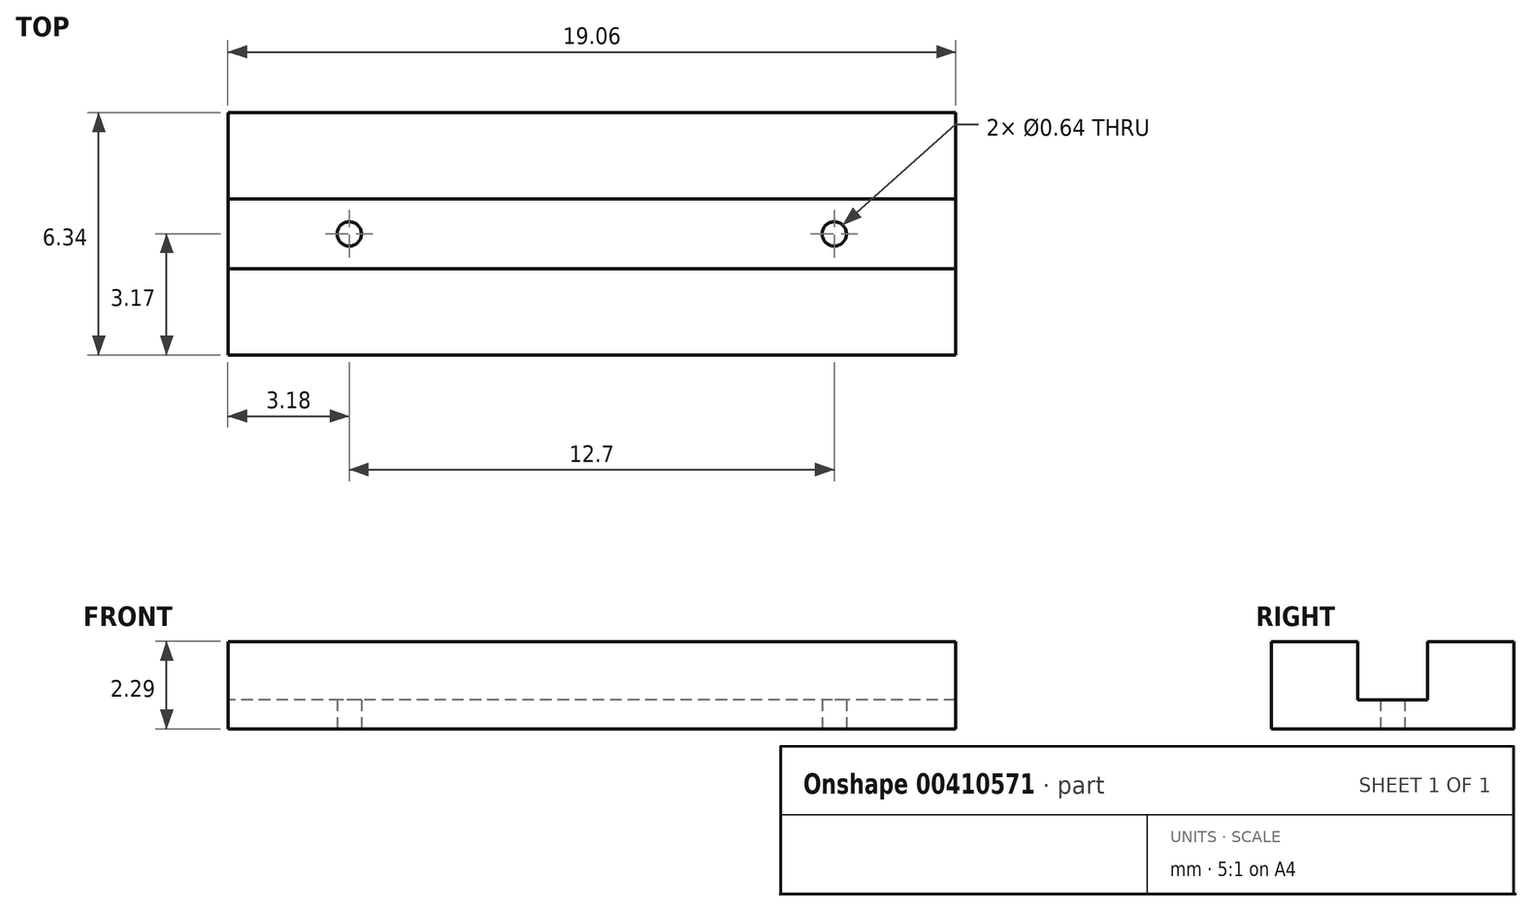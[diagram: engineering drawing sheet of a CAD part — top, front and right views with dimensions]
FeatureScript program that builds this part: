
annotation { "Feature Type Name" : "Feature", "Feature Type Description" : "" }
export const myFeature = defineFeature(function(context is Context, id is Id, definition is map)
    precondition{}
    {
        {
            var Q0;
            Q0=qCreatedBy(makeId("Top.planeOp"),FACE);
            var sketch = newSketch(context, id + "F0", { "sketchPlane" : qUnion([Q0])});
            skLineSegment(sketch, "E0.bottom", {"start": v(9.53, 3.18) * mm, "end": v(-9.53, 3.18) * mm});
            skLineSegment(sketch, "E0.top", {"start": v(9.53, -3.18) * mm, "end": v(-9.53, -3.18) * mm});
            skLineSegment(sketch, "E0.left", {"start": v(9.53, 3.17) * mm, "end": v(9.53, -3.18) * mm});
            skLineSegment(sketch, "E0.right", {"start": v(-9.53, 3.17) * mm, "end": v(-9.53, -3.18) * mm});
            skPoint(sketch, "E0.middle", {"position": v(0, 0) * mm});
            skLineSegment(sketch, "E1.bottom", {"start": v(9.53, 0.91) * mm, "end": v(-9.53, 0.91) * mm});
            skLineSegment(sketch, "E1.top", {"start": v(9.53, -0.91) * mm, "end": v(-9.53, -0.91) * mm});
            skLineSegment(sketch, "E1.left", {"start": v(9.53, 0.91) * mm, "end": v(9.53, -0.91) * mm});
            skLineSegment(sketch, "E1.right", {"start": v(-9.53, 0.91) * mm, "end": v(-9.53, -0.91) * mm});
            skCircle(sketch, "E2", {"center": v(6.35, 0) * mm, "radius": 0.32 * mm});
            skCircle(sketch, "E3", {"center": v(-6.35, 0) * mm, "radius": 0.32 * mm});
            skSolve(sketch);
        }
        {
            var Q0;
            Q0=makeQuery(id+"F0.imprint","IMPRINT",FACE,{"disambiguationData":[TD([[makeQuery(id+"F0.imprint","IMPRINT",EDGE,{"derivedFrom":sQuery(id+"F0.wireOp",EDGE,"E1.bottom")}),1.0]])]});
            extrude(context, id + "F1", {"entities" : qUnion([Q0]), "depth" : 0.76 * mm});
        }
        {
            var Q0;
            {var subQ0=sQuery(id+"F0.wireOp",EDGE,"E0.top");Q0=makeQuery(id+"F0.imprint","IMPRINT",FACE,{"disambiguationData":[TD([[makeQuery(id+"F0.imprint","IMPRINT",EDGE,{"derivedFrom":subQ0}),-1.0]])]});}
            var Q1;
            {var subQ0=sQuery(id+"F0.wireOp",EDGE,"E0.bottom");Q1=makeQuery(id+"F0.imprint","IMPRINT",FACE,{"disambiguationData":[TD([[makeQuery(id+"F0.imprint","IMPRINT",EDGE,{"derivedFrom":subQ0}),1.0]])]});}
            extrude(context, id + "F2", {"entities" : qUnion([Q0, Q1]), "operationType" : NewBodyOperationType.ADD, "depth" : 2.3 * mm});
        }
    });
